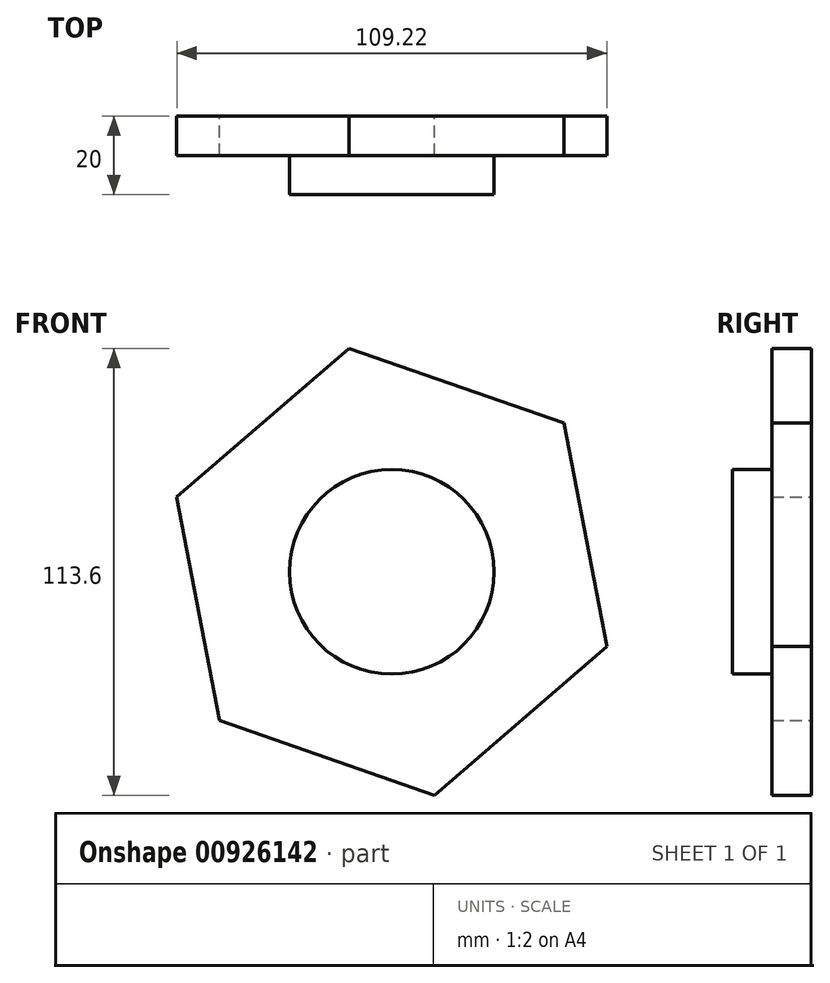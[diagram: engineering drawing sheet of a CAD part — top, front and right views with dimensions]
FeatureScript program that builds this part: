
annotation { "Feature Type Name" : "Feature", "Feature Type Description" : "" }
export const myFeature = defineFeature(function(context is Context, id is Id, definition is map)
    precondition{}
    {
        {
            var Q0;
            Q0=qCreatedBy(makeId("Front.planeOp"),FACE);
            var sketch = newSketch(context, id + "F0", { "sketchPlane" : qUnion([Q0])});
            skCircle(sketch, "E0.cCircle", {"center": v(0, 0) * mm, "radius": 57.83 * mm, "construction": true});
            skLineSegment(sketch, "E0.0", {"start": v(54.61, -19) * mm, "end": v(10.84, -56.8) * mm});
            skLineSegment(sketch, "E0.1", {"start": v(10.84, -56.8) * mm, "end": v(-43.77, -37.8) * mm});
            skLineSegment(sketch, "E0.2", {"start": v(-43.77, -37.8) * mm, "end": v(-54.61, 19) * mm});
            skLineSegment(sketch, "E0.3", {"start": v(-54.61, 19) * mm, "end": v(-10.84, 56.8) * mm});
            skLineSegment(sketch, "E0.4", {"start": v(-10.84, 56.8) * mm, "end": v(43.77, 37.8) * mm});
            skLineSegment(sketch, "E0.5", {"start": v(43.77, 37.8) * mm, "end": v(54.61, -19) * mm});
            skSolve(sketch);
        }
        {
            var Q0;
            Q0=makeQuery(id+"F0.imprint","IMPRINT",FACE,{"disambiguationData":[TD([[makeQuery(id+"F0.imprint","IMPRINT",EDGE,{"derivedFrom":sQuery(id+"F0.wireOp",EDGE,"E0.0")}),-1.0]])]});
            extrude(context, id + "F1", {"entities" : qUnion([Q0]), "depth" : 10 * mm, "offsetDistance" : 25.4 * mm});
        }
        {
            var Q0;
            Q0=qCreatedBy(makeId("Front.planeOp"),FACE);
            var sketch = newSketch(context, id + "F2", { "sketchPlane" : qUnion([Q0])});
            skCircle(sketch, "E1", {"center": v(0, 0) * mm, "radius": 25.99 * mm});
            skSolve(sketch);
        }
        {
            var Q0;
            Q0 = qSketchRegion(id + "F2", true);
            extrude(context, id + "F3", {"entities" : qUnion([Q0]), "operationType" : NewBodyOperationType.ADD, "depth" : 20 * mm, "offsetDistance" : 25.4 * mm});
        }
    });
